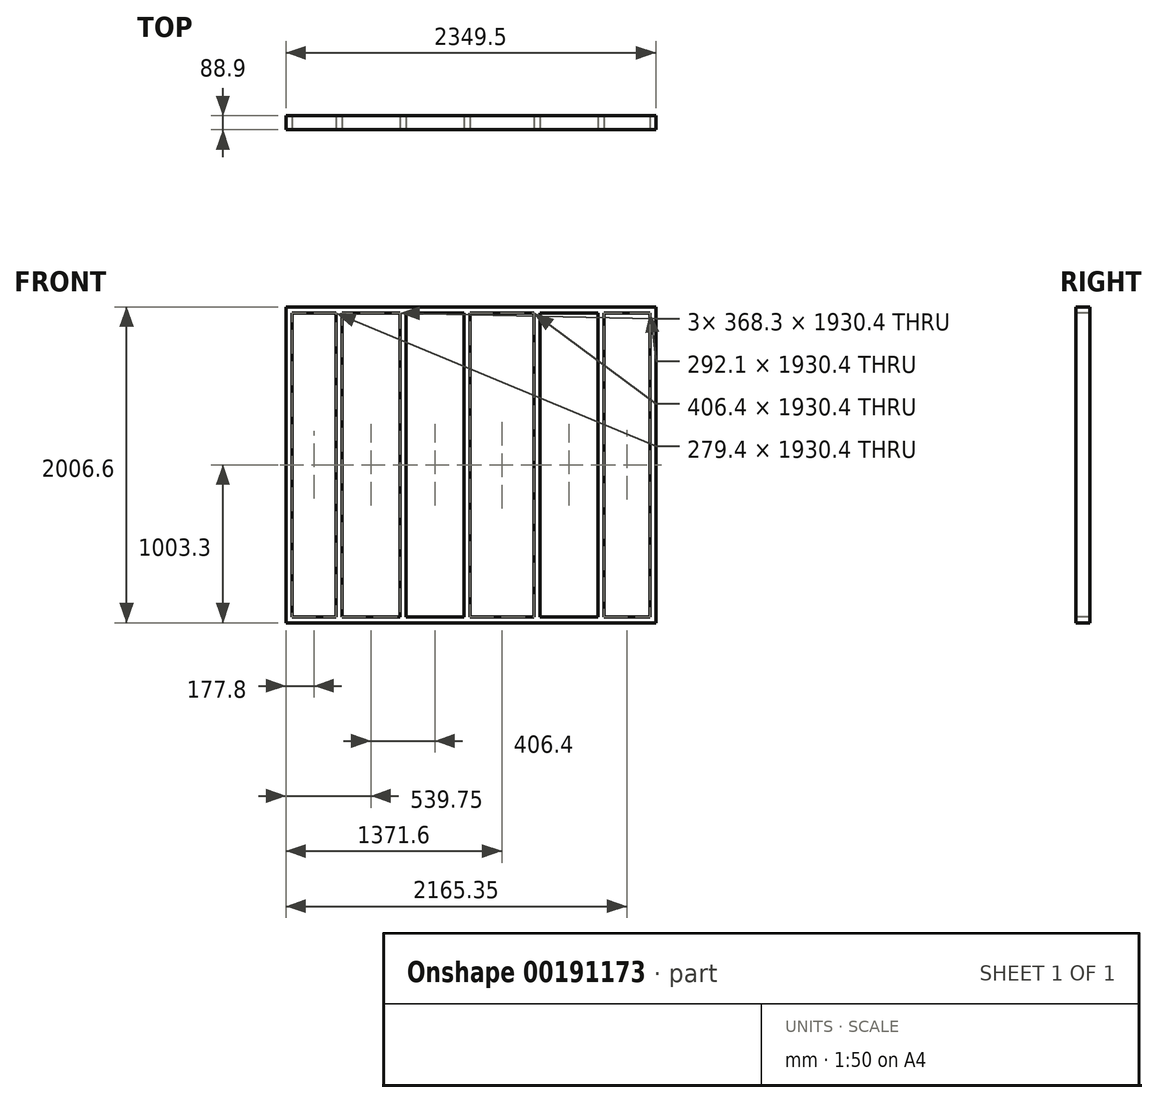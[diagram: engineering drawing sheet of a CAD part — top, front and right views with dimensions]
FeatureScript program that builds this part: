
annotation { "Feature Type Name" : "Feature", "Feature Type Description" : "" }
export const myFeature = defineFeature(function(context is Context, id is Id, definition is map)
    precondition{}
    {
        {
            var Q0;
            Q0=qCreatedBy(makeId("Top.planeOp"),FACE);
            var sketch = newSketch(context, id + "F0", { "sketchPlane" : qUnion([Q0])});
            skLineSegment(sketch, "E0.bottom", {"start": v(1174.75, -44.45) * mm, "end": v(-1174.75, -44.45) * mm});
            skLineSegment(sketch, "E0.top", {"start": v(1174.75, 44.45) * mm, "end": v(-1174.75, 44.45) * mm});
            skLineSegment(sketch, "E0.left", {"start": v(1174.75, -44.45) * mm, "end": v(1174.75, 44.45) * mm});
            skLineSegment(sketch, "E0.right", {"start": v(-1174.75, -44.45) * mm, "end": v(-1174.75, 44.45) * mm});
            skPoint(sketch, "E0.middle", {"position": v(0, 0) * mm});
            skSolve(sketch);
        }
        {
            var Q0;
            Q0 = qSketchRegion(id + "F0", true);
            extrude(context, id + "F1", {"entities" : qUnion([Q0]), "depth" : 38.1 * mm});
        }
        {
            var Q0;
            Q0=makeQuery(id+"F1.opExtrude","CAP_FACE",FACE,{"disambiguationData":[OSD([sQuery(id+"F0.wireOp",EDGE,"E0.bottom"),sQuery(id+"F0.wireOp",EDGE,"E0.top"),sQuery(id+"F0.wireOp",EDGE,"E0.left"),sQuery(id+"F0.wireOp",EDGE,"E0.right")])],"isStart":false});
            var sketch = newSketch(context, id + "F2", { "sketchPlane" : qUnion([Q0])});
            skLineSegment(sketch, "E1.bottom", {"start": v(-1174.75, 44.45) * mm, "end": v(-1136.65, 44.45) * mm});
            skLineSegment(sketch, "E1.top", {"start": v(-1174.75, -44.45) * mm, "end": v(-1136.65, -44.45) * mm});
            skLineSegment(sketch, "E1.left", {"start": v(-1174.75, 44.45) * mm, "end": v(-1174.75, -44.45) * mm});
            skLineSegment(sketch, "E1.right", {"start": v(-1136.65, 44.45) * mm, "end": v(-1136.65, -44.45) * mm});
            skLineSegment(sketch, "E2.bottom", {"start": v(-857.25, 44.45) * mm, "end": v(-819.15, 44.45) * mm});
            skLineSegment(sketch, "E2.top", {"start": v(-857.25, -44.45) * mm, "end": v(-819.15, -44.45) * mm});
            skLineSegment(sketch, "E2.left", {"start": v(-857.25, 44.45) * mm, "end": v(-857.25, -44.45) * mm});
            skLineSegment(sketch, "E2.right", {"start": v(-819.15, 44.45) * mm, "end": v(-819.15, -44.45) * mm});
            skLineSegment(sketch, "E3.bottom", {"start": v(-450.85, 44.45) * mm, "end": v(-412.75, 44.45) * mm});
            skLineSegment(sketch, "E3.top", {"start": v(-450.85, -44.45) * mm, "end": v(-412.75, -44.45) * mm});
            skLineSegment(sketch, "E3.left", {"start": v(-450.85, 44.45) * mm, "end": v(-450.85, -44.45) * mm});
            skLineSegment(sketch, "E3.right", {"start": v(-412.75, 44.45) * mm, "end": v(-412.75, -44.45) * mm});
            skLineSegment(sketch, "E4.bottom", {"start": v(-44.45, 44.45) * mm, "end": v(-6.35, 44.45) * mm});
            skLineSegment(sketch, "E4.top", {"start": v(-44.45, -44.45) * mm, "end": v(-6.35, -44.45) * mm});
            skLineSegment(sketch, "E4.left", {"start": v(-44.45, 44.45) * mm, "end": v(-44.45, -44.45) * mm});
            skLineSegment(sketch, "E4.right", {"start": v(-6.35, 44.45) * mm, "end": v(-6.35, -44.45) * mm});
            skLineSegment(sketch, "E5.bottom", {"start": v(400.05, 44.45) * mm, "end": v(438.15, 44.45) * mm});
            skLineSegment(sketch, "E5.top", {"start": v(400.05, -44.45) * mm, "end": v(438.15, -44.45) * mm});
            skLineSegment(sketch, "E5.left", {"start": v(400.05, 44.45) * mm, "end": v(400.05, -44.45) * mm});
            skLineSegment(sketch, "E5.right", {"start": v(438.15, 44.45) * mm, "end": v(438.15, -44.45) * mm});
            skLineSegment(sketch, "E6.bottom", {"start": v(806.45, 44.45) * mm, "end": v(844.55, 44.45) * mm});
            skLineSegment(sketch, "E6.top", {"start": v(806.45, -44.45) * mm, "end": v(844.55, -44.45) * mm});
            skLineSegment(sketch, "E6.left", {"start": v(806.45, 44.45) * mm, "end": v(806.45, -44.45) * mm});
            skLineSegment(sketch, "E6.right", {"start": v(844.55, 44.45) * mm, "end": v(844.55, -44.45) * mm});
            skLineSegment(sketch, "E7.bottom", {"start": v(1174.75, 44.45) * mm, "end": v(1136.65, 44.45) * mm});
            skLineSegment(sketch, "E7.top", {"start": v(1174.75, -44.45) * mm, "end": v(1136.65, -44.45) * mm});
            skLineSegment(sketch, "E7.left", {"start": v(1174.75, 44.45) * mm, "end": v(1174.75, -44.45) * mm});
            skLineSegment(sketch, "E7.right", {"start": v(1136.65, 44.45) * mm, "end": v(1136.65, -44.45) * mm});
            skSolve(sketch);
        }
        {
            var Q0;
            Q0 = qSketchRegion(id + "F2", true);
            extrude(context, id + "F3", {"entities" : qUnion([Q0]), "operationType" : NewBodyOperationType.ADD, "depth" : 1930.4 * mm});
        }
        {
            var Q0;
            Q0=makeQuery(id+"F3.boolean.opBoolean","MERGE",FACE,{"derivedFrom":[makeQuery(id+"F1.opExtrude","SWEPT_FACE",FACE,{"disambiguationData":[OSD([sQuery(id+"F0.wireOp",EDGE,"E0.bottom")])]}),makeQuery(id+"F3.opExtrude","SWEPT_FACE",FACE,{"disambiguationData":[OSD([sQuery(id+"F2.wireOp",EDGE,"E1.top")])]}),makeQuery(id+"F3.opExtrude","SWEPT_FACE",FACE,{"disambiguationData":[OSD([sQuery(id+"F2.wireOp",EDGE,"E2.top")])]}),makeQuery(id+"F3.opExtrude","SWEPT_FACE",FACE,{"disambiguationData":[OSD([sQuery(id+"F2.wireOp",EDGE,"E3.top")])]}),makeQuery(id+"F3.opExtrude","SWEPT_FACE",FACE,{"disambiguationData":[OSD([sQuery(id+"F2.wireOp",EDGE,"E4.top")])]}),makeQuery(id+"F3.opExtrude","SWEPT_FACE",FACE,{"disambiguationData":[OSD([sQuery(id+"F2.wireOp",EDGE,"E5.top")])]}),makeQuery(id+"F3.opExtrude","SWEPT_FACE",FACE,{"disambiguationData":[OSD([sQuery(id+"F2.wireOp",EDGE,"E6.top")])]}),makeQuery(id+"F3.opExtrude","SWEPT_FACE",FACE,{"disambiguationData":[OSD([sQuery(id+"F2.wireOp",EDGE,"E7.top")])]})]});
            var sketch = newSketch(context, id + "F4", { "sketchPlane" : qUnion([Q0])});
            skLineSegment(sketch, "E8.bottom", {"start": v(1174.75, 1968.5) * mm, "end": v(-1174.75, 1968.5) * mm});
            skLineSegment(sketch, "E8.top", {"start": v(1174.75, 2006.6) * mm, "end": v(-1174.75, 2006.6) * mm});
            skLineSegment(sketch, "E8.left", {"start": v(1174.75, 1968.5) * mm, "end": v(1174.75, 2006.6) * mm});
            skLineSegment(sketch, "E8.right", {"start": v(-1174.75, 1968.5) * mm, "end": v(-1174.75, 2006.6) * mm});
            skSolve(sketch);
        }
        {
            var Q0;
            Q0 = qSketchRegion(id + "F4", true);
            extrude(context, id + "F5", {"entities" : qUnion([Q0]), "operationType" : NewBodyOperationType.ADD, "oppositeDirection" : true, "depth" : 88.9 * mm});
        }
    });
